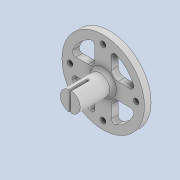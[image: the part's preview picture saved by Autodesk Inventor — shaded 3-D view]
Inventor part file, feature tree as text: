
AUTODESK INVENTOR PART (.ipt)
format: ipt  version: 2020 (Build 240168000, 168)  size: 259,072 bytes
history: native  units: mm
features: sketch x7, extrude x6, fillet x4, projected_geometry x4, other x4, hole x1, pattern_circular x1, thicken_offset x1, chamfer x1, reference x1
ambient origin geometry x8: Origin, YZ Plane, XZ Plane, XY Plane, X Axis, Y Axis, Z Axis, Center Point
bodies: Solid1 (feature_tree)
feature tree (30):
  extrude  "Extrusion1"  Depth=5.0mm
  hole  "Hole1"  [1 undecoded]
  extrude  "Extrusion2"  Depth=2.0mm
  fillet  "Fillet1"  Radius=1.0mm
  fillet  "Fillet2"  Radius=2.0mm
  extrude  "Extrusion3"  Depth=25.0mm
  extrude  "Extrusion4"  Depth=2.0mm TaperAngle=0.0deg
  pattern_circular  "Circular Pattern1"  Count=4 Angle=360.0deg
  fillet  "Fillet3"  Radius=1.0mm
  extrude  "Extrusion5"  Depth=4.0mm
  thicken_offset  "Thicken1"
  extrude  "Extrusion6"  Depth=0.4mm
  fillet  "Fillet4"  Radius=12.0mm
  chamfer  "Chamfer1"  Distance=5.5mm
  sketch  "Sketch1"  dims[d0=5.0mm d1=5.0mm]
  reference  "Reference1"
  sketch  "Sketch2"  dims[d2=2.0mm d3=0.0mm]
  projected_geometry  "Projected Loop1"
  sketch  "Sketch3"  dims[d4=1.65mm d5=6.0mm d6=4.0mm d7=2.0mm d8=90.0deg d9=5.0mm d10=0.0mm d11=6.0mm]
  sketch  "Sketch4"  dims[d12=6.0mm d13=0.0mm d14=2.0mm d15=1.0mm d16=2.0mm]
  sketch  "Sketch5"  dims[d17=12.0mm d18=0.0mm d19=25.0mm]
  projected_geometry  "Projected Loop2"
  sketch  "Sketch6"  dims[d20=20.0mm d21=2.0mm d22=0.0mm d23=40.0mm d24=360.0deg d26=1.0mm]
  projected_geometry  "Projected Loop3"
  sketch  "Sketch7"  dims[d27=10.0mm d28=0.0mm d29=4.0mm d30=6.0mm d31=0.4mm d32=12.0mm d33=5.5mm d34=0.0mm d35=0.2mm d36=0.2mm d37=2.0mm d38=45.0deg]
  projected_geometry  "Projected Loop4"
  parser-record x1  (decoder bookkeeping rows leaked as tree rows — omitted from the tree; the rows remain in map.json)
  other  "reducer_1.iam"
  other  "mot_27_ass:1"
  other  "mot_27_1:1"
note: 1 required parameter value undecoded (feature->parameter linkage not recoverable at this tier; creation-order binding heuristic only, values carry confidence <= 0.55)
note: 1 file-system path scrubbed to <path> (originals preserved in map.json)
